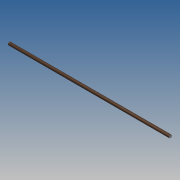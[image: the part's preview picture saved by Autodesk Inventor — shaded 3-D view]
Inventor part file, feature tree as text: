
AUTODESK INVENTOR PART (.ipt)
format: ipt  version: 2014 SP1 (Build 180222100, 222)  size: 125,440 bytes
history: native  units: in
note: dims shown in document units (in); Inventor stores cm internally (conversion verified against a paired STEP export)
features: extrude x1, sketch x1
ambient origin geometry x8: Origin, YZ Plane, XZ Plane, XY Plane, X Axis, Y Axis, Z Axis, Center Point
bodies: Body1 (feature_tree)
feature tree (2):
  extrude  "Extrusion2"  Depth=26.0in TaperAngle=0.0deg
  sketch  "Sketch2"  dims[d3=0.4724in d4=26.0in d5=0.0in]
